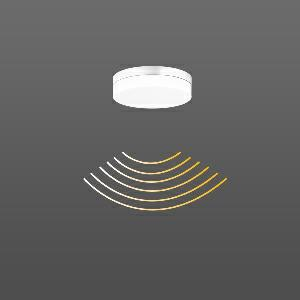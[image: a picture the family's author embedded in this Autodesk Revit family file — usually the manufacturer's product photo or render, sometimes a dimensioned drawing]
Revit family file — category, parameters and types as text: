
# Revit family: flat_slim_round_312132_002_19_d3d3
name_source: partatom
category: Lighting Fixtures
units: mm (PartAtom-declared; Revit-internal decimal feet)

## family parameters
Cut with Voids When Loaded = No
Host = Face
Light Source = No
Part Type = Normal
Room Calculation Point = No
Round Connector Dimension = Use Diameter
Shared = No

## types (1)
- FLAT SLIM round (1 x LED Modul 830, 1000 lm, 3000)
    Apparent Load = 12 VA
    CIE Flux Codes = 42 72 91 89 100
    Color Rendering = 80
    Color Temperature = 3000
    Default Elevation = 1800 mm
    Height = 63 mm
    Lamp = 1 x LED Modul 830
    Lamp Light Flux = 1000 lm
    Lamp count = 1
    Length = 230 mm
    Lifetime = 50000 h
    Luminous efficacy = 83 lm/W
    Manufacturer = RZB
    ModVariant = No
    Model = 312132.002.19
    Mounting Place = Ceiling, Wall
    Mounting Type = Surface mounted
    Number of Poles = 1
    OnlyDefault = Yes
    Power Factor = 1
    Product Name = FLAT SLIM round
    Product group = Surface mounted ceiling and wall luminaires
    ProductGroupID = 305
    Protection Class = Protection class I
    Protection Degree = IP 65
    RLX_Detail_Level = 1
    RLX_Emergency_Light_Flux = 0 lm
    RLX_Emergency_Type = 0
    RLX_Emergency_Type_DB = No
    RlxData = <blob elided: 32185 chars, md5=bc9b1758>
    Socket = socket
    Standby Power = 0 W
    System Light Flux = 1000 lm
    System Power = 12 W
    Type Comments = Product without accessories
    Type Image = 312132.002.19.jpg
    URL = http://relux.com
    VarID = ---
    Voltage = 230 V
    Voltage Range = 220-240 V
    Weight = 0.00 kg
    Width = 0 mm  [stored 0 ft]

note: [stored X ft] marks values corroborated as IEEE doubles in the binary element streams (Revit-internal decimal feet)

## geometry (parser evidence)
native form markers: Blend x4, Sweep x11
no freeform markers — native parametric forms only
